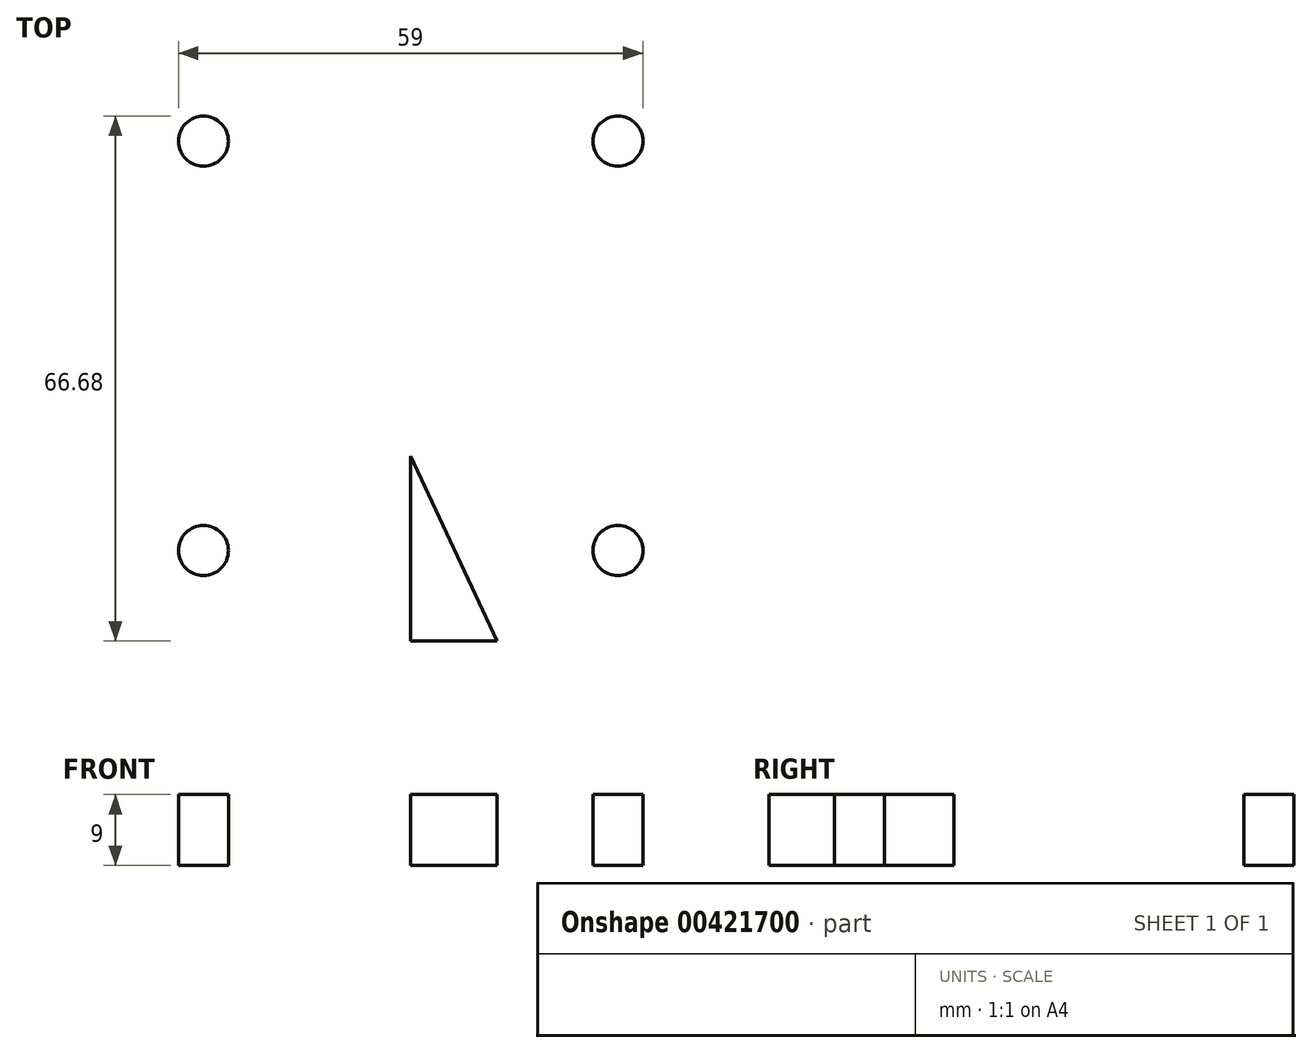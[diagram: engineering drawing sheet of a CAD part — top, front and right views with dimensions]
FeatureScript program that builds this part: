
annotation { "Feature Type Name" : "Feature", "Feature Type Description" : "" }
export const myFeature = defineFeature(function(context is Context, id is Id, definition is map)
    precondition{}
    {
        {
            var Q0;
            Q0=qCreatedBy(makeId("Top.planeOp"),FACE);
            var sketch = newSketch(context, id + "F0", { "sketchPlane" : qUnion([Q0])});
            skLineSegment(sketch, "E0", {"start": v(0, 60) * mm, "end": v(0, -60) * mm});
            skLineSegment(sketch, "E1", {"start": v(-70, 0) * mm, "end": v(70, 0) * mm});
            skLineSegment(sketch, "E2", {"start": v(-29.5, 37.5) * mm, "end": v(29.5, 37.5) * mm});
            skLineSegment(sketch, "E3", {"start": v(-29.5, -37.5) * mm, "end": v(10.96, -37.5) * mm});
            skCircle(sketch, "E4", {"center": v(-26.32, 26) * mm, "radius": 3.17 * mm});
            skCircle(sketch, "E5", {"center": v(-26.32, -26) * mm, "radius": 3.17 * mm});
            skCircle(sketch, "E6", {"center": v(26.32, -26) * mm, "radius": 3.17 * mm});
            skCircle(sketch, "E7", {"center": v(26.32, 26) * mm, "radius": 3.17 * mm});
            skArc(sketch, "E8", {"start": v(9.36, -10.41) * mm, "mid": v(-5.01, 13.07) * mm, "end": v(0, -14) * mm});
            skLineSegment(sketch, "E9", {"start": v(-37.5, -29.5) * mm, "end": v(-37.5, 29.5) * mm});
            skLineSegment(sketch, "E10", {"start": v(37.5, -29.5) * mm, "end": v(37.5, 29.5) * mm});
            skArc(sketch, "E11", {"start": v(-29.5, 37.5) * mm, "mid": v(-35.16, 35.16) * mm, "end": v(-37.5, 29.5) * mm});
            skArc(sketch, "E12", {"start": v(37.5, 29.5) * mm, "mid": v(35.16, 35.16) * mm, "end": v(29.5, 37.5) * mm});
            skArc(sketch, "E13", {"start": v(29.5, -37.5) * mm, "mid": v(35.16, -35.16) * mm, "end": v(37.5, -29.5) * mm});
            skArc(sketch, "E14", {"start": v(-37.5, -29.5) * mm, "mid": v(-35.16, -35.16) * mm, "end": v(-29.5, -37.5) * mm});
            skLineSegment(sketch, "E15", {"start": v(0, -14) * mm, "end": v(10.96, -37.5) * mm});
            skLineSegment(sketch, "E16", {"start": v(9.36, -10.41) * mm, "end": v(22, -37.5) * mm});
            skLineSegment(sketch, "E17", {"start": v(22, -37.5) * mm, "end": v(29.5, -37.5) * mm});
            skSolve(sketch);
        }
        {
            var Q0;
            {var subQ0=sQuery(id+"F0.wireOp",EDGE,"E15");Q0=makeQuery(id+"F0.imprint","IMPRINT",FACE,{"disambiguationData":[TD([[makeQuery(id+"F0.imprint","IMPRINT",EDGE,{"derivedFrom":subQ0}),-1.0]])]});}
            var Q1;
            Q1=makeQuery(id+"F0.imprint","IMPRINT",FACE,{"disambiguationData":[TD([[makeQuery(id+"F0.imprint","IMPRINT",EDGE,{"derivedFrom":sQuery(id+"F0.wireOp",EDGE,"E5")}),1.0]])]});
            var Q2;
            Q2=makeQuery(id+"F0.imprint","IMPRINT",FACE,{"disambiguationData":[TD([[makeQuery(id+"F0.imprint","IMPRINT",EDGE,{"derivedFrom":sQuery(id+"F0.wireOp",EDGE,"E6")}),1.0]])]});
            var Q3;
            Q3=makeQuery(id+"F0.imprint","IMPRINT",FACE,{"disambiguationData":[TD([[makeQuery(id+"F0.imprint","IMPRINT",EDGE,{"derivedFrom":sQuery(id+"F0.wireOp",EDGE,"E7")}),1.0]])]});
            var Q4;
            Q4=makeQuery(id+"F0.imprint","IMPRINT",FACE,{"disambiguationData":[TD([[makeQuery(id+"F0.imprint","IMPRINT",EDGE,{"derivedFrom":sQuery(id+"F0.wireOp",EDGE,"E4")}),1.0]])]});
            extrude(context, id + "F1", {"entities" : qUnion([Q0, Q1, Q2, Q3, Q4]), "depth" : 9 * mm});
        }
    });
